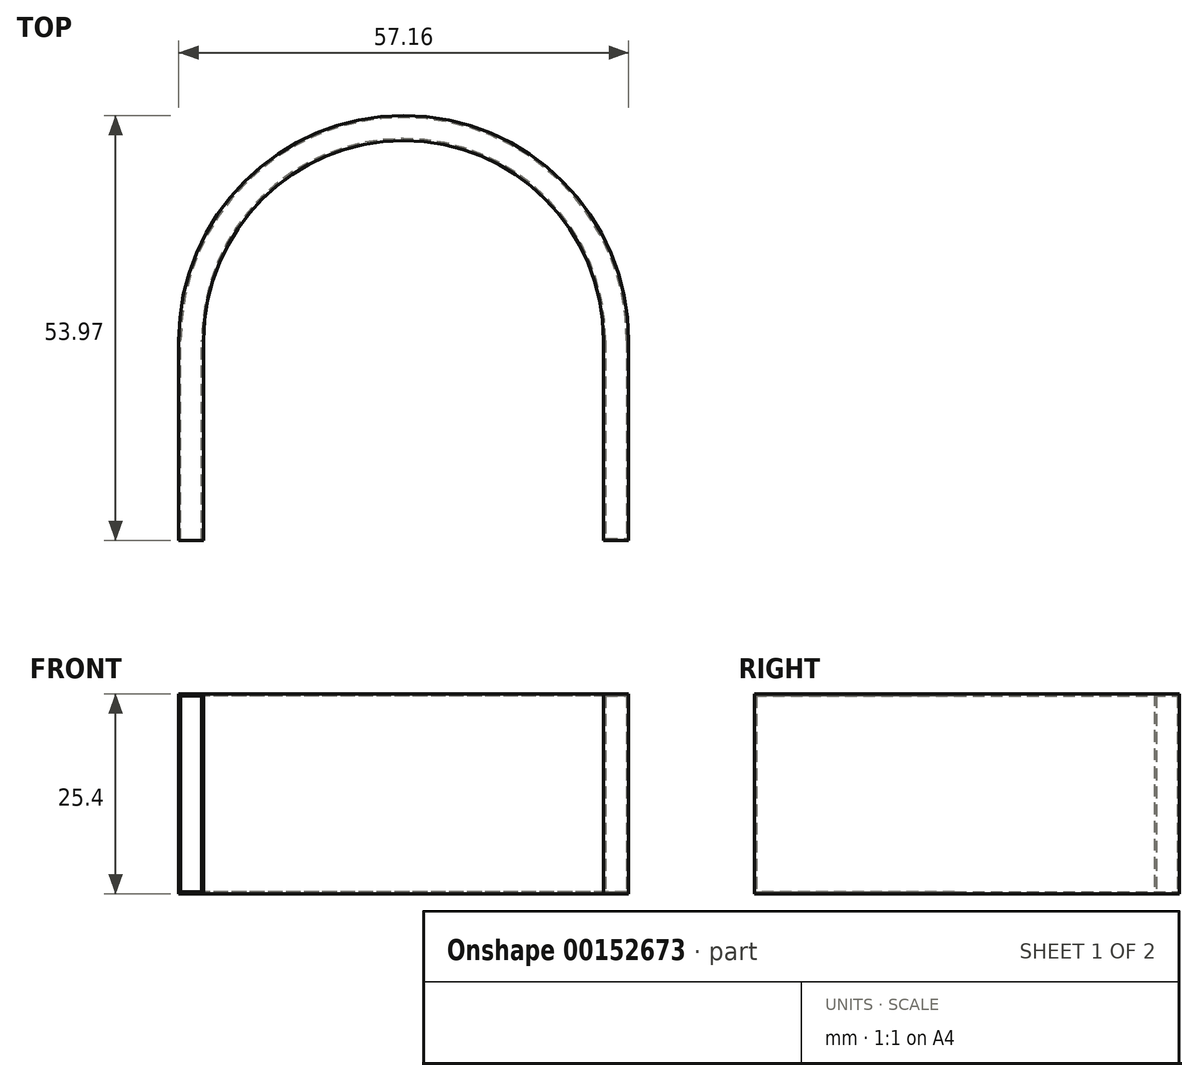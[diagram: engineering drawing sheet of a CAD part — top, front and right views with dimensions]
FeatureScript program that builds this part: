
annotation { "Feature Type Name" : "Feature", "Feature Type Description" : "" }
export const myFeature = defineFeature(function(context is Context, id is Id, definition is map)
    precondition{}
    {
        {
            var Q0;
            Q0=qCreatedBy(makeId("Top.planeOp"),FACE);
            var sketch = newSketch(context, id + "F0", { "sketchPlane" : qUnion([Q0])});
            skLineSegment(sketch, "E0.bottom", {"start": v(0, 0) * mm, "end": v(-3.18, 0) * mm});
            skLineSegment(sketch, "E0.top", {"start": v(0, 25.4) * mm, "end": v(-3.18, 25.4) * mm, "construction": true});
            skLineSegment(sketch, "E0.left", {"start": v(0, 0) * mm, "end": v(0, 25.4) * mm});
            skLineSegment(sketch, "E0.right", {"start": v(-3.17, 0) * mm, "end": v(-3.18, 25.4) * mm});
            skLineSegment(sketch, "E1", {"start": v(0, 25.4) * mm, "end": v(50.8, 25.4) * mm, "construction": true});
            skLineSegment(sketch, "E2.bottom", {"start": v(50.8, 25.4) * mm, "end": v(53.97, 25.4) * mm, "construction": true});
            skLineSegment(sketch, "E2.top", {"start": v(50.8, 0) * mm, "end": v(53.98, 0) * mm});
            skLineSegment(sketch, "E2.left", {"start": v(50.8, 25.4) * mm, "end": v(50.8, 0) * mm});
            skLineSegment(sketch, "E2.right", {"start": v(53.98, 25.4) * mm, "end": v(53.98, 0) * mm});
            skArc(sketch, "E3", {"start": v(50.8, 25.4) * mm, "mid": v(25.4, 50.8) * mm, "end": v(0, 25.4) * mm});
            skArc(sketch, "E4", {"start": v(53.98, 25.4) * mm, "mid": v(25.4, 53.98) * mm, "end": v(-3.18, 25.4) * mm});
            skSolve(sketch);
        }
        {
            var Q0;
            Q0=qSketchRegion(id+"F0",true);
            extrude(context, id + "F1", {"entities" : qUnion([Q0]), "depth" : 25.4 * mm});
        }
        {
            var Q0;
            Q0=makeQuery(id+"F1.opExtrude","SWEPT_FACE",FACE,{"disambiguationData":[OSD([sQuery(id+"F0.wireOp",EDGE,"E0.bottom")])]});
            shell(context, id + "F2", {"entities" : qUnion([Q0]), "thickness" : 0.25 * mm});
        }
    });
